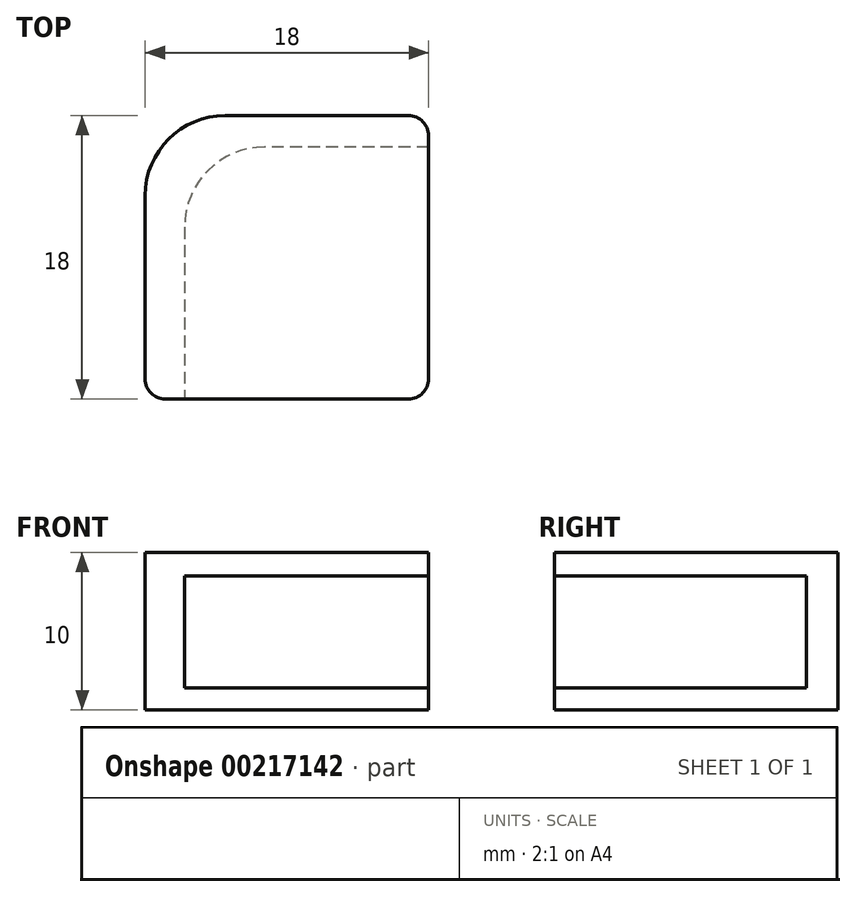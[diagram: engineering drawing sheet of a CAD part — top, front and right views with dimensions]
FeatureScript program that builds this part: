
annotation { "Feature Type Name" : "Feature", "Feature Type Description" : "" }
export const myFeature = defineFeature(function(context is Context, id is Id, definition is map)
    precondition{}
    {
        {
            var Q0;
            Q0=qCreatedBy(makeId("Top.planeOp"),FACE);
            var sketch = newSketch(context, id + "F0", { "sketchPlane" : qUnion([Q0])});
            skLineSegment(sketch, "E0.bottom", {"start": v(-9, 9) * mm, "end": v(9, 9) * mm});
            skLineSegment(sketch, "E0.top", {"start": v(-9, -9) * mm, "end": v(9, -9) * mm});
            skLineSegment(sketch, "E0.left", {"start": v(-9, 9) * mm, "end": v(-9, -9) * mm});
            skLineSegment(sketch, "E0.right", {"start": v(9, 9) * mm, "end": v(9, -9) * mm});
            skPoint(sketch, "E0.middle", {"position": v(0, 0) * mm});
            skSolve(sketch);
        }
        {
            var Q0;
            Q0 = qSketchRegion(id + "F0", true);
            extrude(context, id + "F1", {"entities" : qUnion([Q0]), "depth" : 10 * mm});
        }
        {
            var Q0;
            Q0=makeQuery(id+"F1.opExtrude","SWEPT_FACE",FACE,{"disambiguationData":[OSD([sQuery(id+"F0.wireOp",EDGE,"E0.top")])]});
            var sketch = newSketch(context, id + "F2", { "sketchPlane" : qUnion([Q0])});
            skLineSegment(sketch, "E1.bottom", {"start": v(9, 8.5) * mm, "end": v(-6.5, 8.5) * mm});
            skLineSegment(sketch, "E1.top", {"start": v(9, 1.4) * mm, "end": v(-6.5, 1.4) * mm});
            skLineSegment(sketch, "E1.left", {"start": v(9, 8.5) * mm, "end": v(9, 1.4) * mm});
            skLineSegment(sketch, "E1.right", {"start": v(-6.5, 8.5) * mm, "end": v(-6.5, 1.4) * mm});
            skSolve(sketch);
        }
        {
            var Q0;
            Q0=makeQuery(id+"F2.imprint","IMPRINT",FACE,{"disambiguationData":[TD([[makeQuery(id+"F2.imprint","IMPRINT",EDGE,{"derivedFrom":sQuery(id+"F2.wireOp",EDGE,"E1.bottom")}),1.0]])]});
            extrude(context, id + "F3", {"entities" : qUnion([Q0]), "operationType" : NewBodyOperationType.REMOVE, "oppositeDirection" : true, "depth" : 16 * mm});
        }
        {
            var Q0;
            Q0=makeQuery(id+"F1.opExtrude","SWEPT_EDGE",EDGE,{"disambiguationData":[OSD([sQuery(id+"F0.wireOp",EDGE,"E0.bottom"),sQuery(id+"F0.wireOp",EDGE,"E0.left")])]});
            fillet(context, id + "F4", {"entities" : qUnion([Q0]), "radius" : 5.08 * mm, "tangentPropagation" : true, "allowEdgeOverflow" : false});
        }
        {
            var Q0;
            Q0=makeQuery(id+"F3.boolean.opBoolean","COPY",EDGE,{"derivedFrom":makeQuery(id+"F3.opExtrude","CAP_EDGE",EDGE,{"disambiguationData":[OSD([sQuery(id+"F2.wireOp",EDGE,"E1.right")])],"isStart":false})});
            fillet(context, id + "F5", {"entities" : qUnion([Q0]), "radius" : 5.08 * mm, "tangentPropagation" : true, "allowEdgeOverflow" : false});
        }
        {
            var Q0;
            Q0=makeQuery(id+"F1.opExtrude","SWEPT_EDGE",EDGE,{"disambiguationData":[OSD([sQuery(id+"F0.wireOp",EDGE,"E0.top"),sQuery(id+"F0.wireOp",EDGE,"E0.left")])]});
            var Q1;
            Q1=makeQuery(id+"F1.opExtrude","SWEPT_EDGE",EDGE,{"disambiguationData":[OSD([sQuery(id+"F0.wireOp",EDGE,"E0.bottom"),sQuery(id+"F0.wireOp",EDGE,"E0.right")])]});
            var Q2;
            {var subQ0=sQuery(id+"F0.wireOp",EDGE,"E0.right");var subQ1=sQuery(id+"F0.wireOp",EDGE,"E0.top");Q2=makeQuery(id+"F3.boolean.opBoolean","SPLIT",EDGE,{"disambiguationData":[TD([makeQuery(id+"F3.opExtrude","SWEPT_FACE",FACE,{"disambiguationData":[OSD([sQuery(id+"F2.wireOp",EDGE,"E1.bottom")])]})])],"derivedFrom":makeQuery(id+"F1.opExtrude","SWEPT_EDGE",EDGE,{"disambiguationData":[OSD([subQ1,subQ0])]})});}
            var Q3;
            {var subQ0=sQuery(id+"F0.wireOp",EDGE,"E0.right");var subQ1=sQuery(id+"F0.wireOp",EDGE,"E0.top");Q3=makeQuery(id+"F3.boolean.opBoolean","SPLIT",EDGE,{"disambiguationData":[TD([makeQuery(id+"F3.opExtrude","SWEPT_FACE",FACE,{"disambiguationData":[OSD([sQuery(id+"F2.wireOp",EDGE,"E1.top")])]})])],"derivedFrom":makeQuery(id+"F1.opExtrude","SWEPT_EDGE",EDGE,{"disambiguationData":[OSD([subQ1,subQ0])]})});}
            fillet(context, id + "F6", {"entities" : qUnion([Q0, Q1, Q2, Q3]), "radius" : 1.27 * mm, "tangentPropagation" : true, "allowEdgeOverflow" : false});
        }
    });
